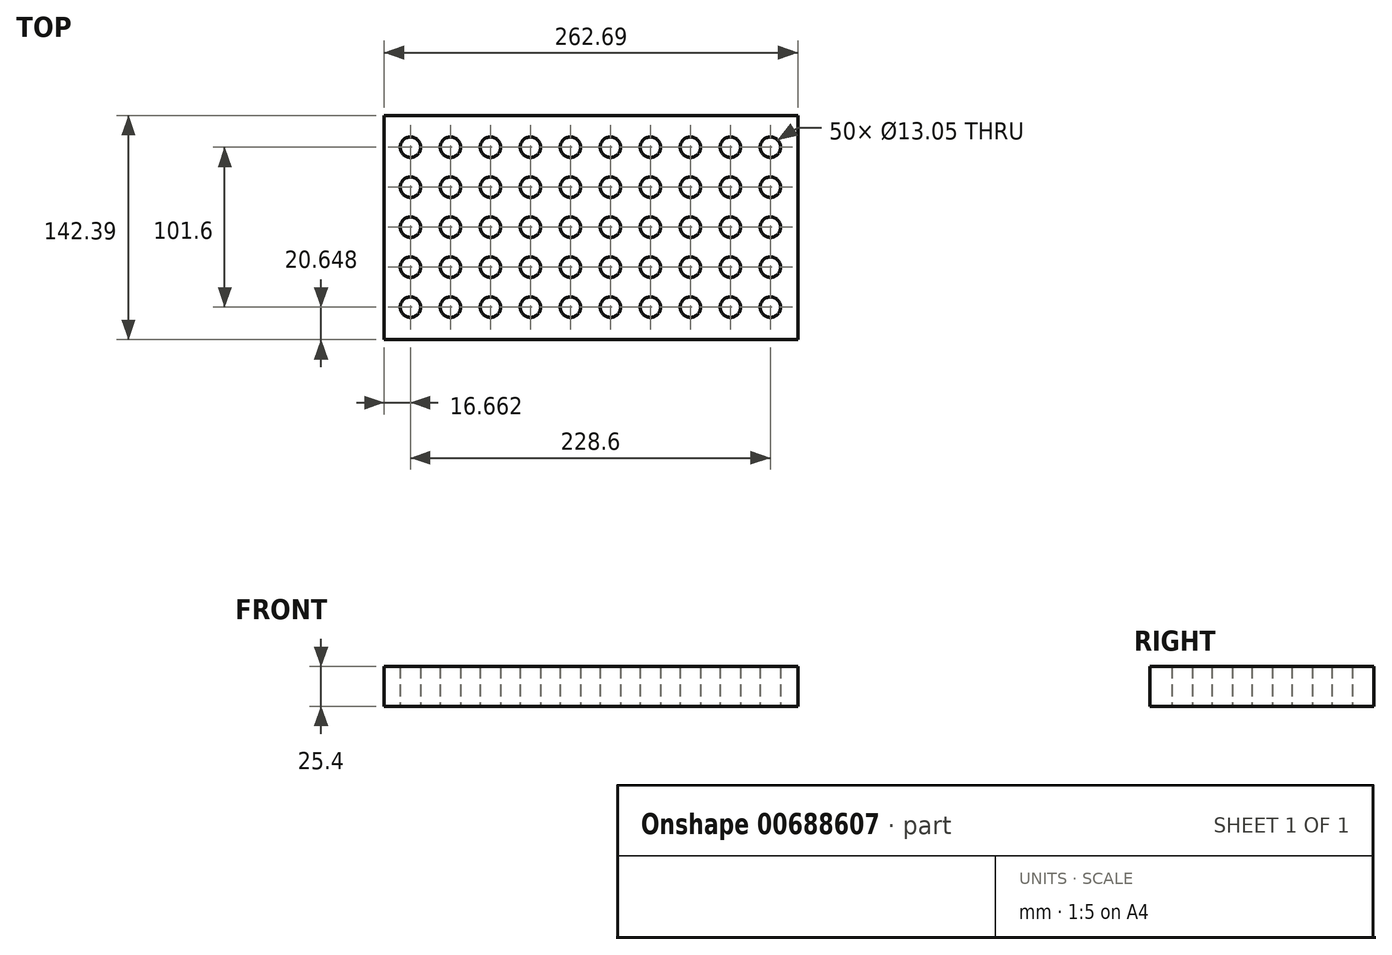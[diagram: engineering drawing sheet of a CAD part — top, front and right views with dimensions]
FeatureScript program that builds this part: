
annotation { "Feature Type Name" : "Feature", "Feature Type Description" : "" }
export const myFeature = defineFeature(function(context is Context, id is Id, definition is map)
    precondition{}
    {
        {
            var Q0;
            Q0=qCreatedBy(makeId("Top.planeOp"),FACE);
            var sketch = newSketch(context, id + "F0", { "sketchPlane" : qUnion([Q0])});
            skLineSegment(sketch, "E0.bottom", {"start": v(-134.73, 82.8) * mm, "end": v(127.96, 82.8) * mm});
            skLineSegment(sketch, "E0.top", {"start": v(-134.73, -59.6) * mm, "end": v(127.96, -59.6) * mm});
            skLineSegment(sketch, "E0.left", {"start": v(-134.73, 82.8) * mm, "end": v(-134.73, -59.6) * mm});
            skLineSegment(sketch, "E0.right", {"start": v(127.96, 82.8) * mm, "end": v(127.96, -59.6) * mm});
            skCircle(sketch, "E1", {"center": v(-118.07, -38.94) * mm, "radius": 6.52 * mm});
            skCircle(sketch, "E2.0.1.0", {"center": v(-118.07, -13.54) * mm, "radius": 6.52 * mm});
            skCircle(sketch, "E2.0.2.0", {"center": v(-118.07, 11.86) * mm, "radius": 6.52 * mm});
            skCircle(sketch, "E2.0.3.0", {"center": v(-118.07, 37.26) * mm, "radius": 6.52 * mm});
            skCircle(sketch, "E2.0.4.0", {"center": v(-118.07, 62.66) * mm, "radius": 6.52 * mm});
            skCircle(sketch, "E2.1.0.0", {"center": v(-92.67, -38.94) * mm, "radius": 6.52 * mm});
            skCircle(sketch, "E2.1.1.0", {"center": v(-92.67, -13.54) * mm, "radius": 6.52 * mm});
            skCircle(sketch, "E2.1.2.0", {"center": v(-92.67, 11.86) * mm, "radius": 6.52 * mm});
            skCircle(sketch, "E2.1.3.0", {"center": v(-92.67, 37.26) * mm, "radius": 6.52 * mm});
            skCircle(sketch, "E2.1.4.0", {"center": v(-92.67, 62.66) * mm, "radius": 6.52 * mm});
            skCircle(sketch, "E2.2.0.0", {"center": v(-67.27, -38.94) * mm, "radius": 6.52 * mm});
            skCircle(sketch, "E2.2.1.0", {"center": v(-67.27, -13.54) * mm, "radius": 6.52 * mm});
            skCircle(sketch, "E2.2.2.0", {"center": v(-67.27, 11.86) * mm, "radius": 6.52 * mm});
            skCircle(sketch, "E2.2.3.0", {"center": v(-67.27, 37.26) * mm, "radius": 6.52 * mm});
            skCircle(sketch, "E2.2.4.0", {"center": v(-67.27, 62.66) * mm, "radius": 6.52 * mm});
            skCircle(sketch, "E2.3.0.0", {"center": v(-41.87, -38.94) * mm, "radius": 6.52 * mm});
            skCircle(sketch, "E2.3.1.0", {"center": v(-41.87, -13.54) * mm, "radius": 6.52 * mm});
            skCircle(sketch, "E2.3.2.0", {"center": v(-41.87, 11.86) * mm, "radius": 6.52 * mm});
            skCircle(sketch, "E2.3.3.0", {"center": v(-41.87, 37.26) * mm, "radius": 6.52 * mm});
            skCircle(sketch, "E2.3.4.0", {"center": v(-41.87, 62.66) * mm, "radius": 6.52 * mm});
            skCircle(sketch, "E2.4.0.0", {"center": v(-16.47, -38.94) * mm, "radius": 6.52 * mm});
            skCircle(sketch, "E2.4.1.0", {"center": v(-16.47, -13.54) * mm, "radius": 6.52 * mm});
            skCircle(sketch, "E2.4.2.0", {"center": v(-16.47, 11.86) * mm, "radius": 6.52 * mm});
            skCircle(sketch, "E2.4.3.0", {"center": v(-16.47, 37.26) * mm, "radius": 6.52 * mm});
            skCircle(sketch, "E2.4.4.0", {"center": v(-16.47, 62.66) * mm, "radius": 6.52 * mm});
            skCircle(sketch, "E2.5.0.0", {"center": v(8.93, -38.94) * mm, "radius": 6.52 * mm});
            skCircle(sketch, "E2.5.1.0", {"center": v(8.93, -13.54) * mm, "radius": 6.52 * mm});
            skCircle(sketch, "E2.5.2.0", {"center": v(8.93, 11.86) * mm, "radius": 6.52 * mm});
            skCircle(sketch, "E2.5.3.0", {"center": v(8.93, 37.26) * mm, "radius": 6.52 * mm});
            skCircle(sketch, "E2.5.4.0", {"center": v(8.93, 62.66) * mm, "radius": 6.52 * mm});
            skCircle(sketch, "E2.6.0.0", {"center": v(34.33, -38.94) * mm, "radius": 6.52 * mm});
            skCircle(sketch, "E2.6.1.0", {"center": v(34.33, -13.54) * mm, "radius": 6.52 * mm});
            skCircle(sketch, "E2.6.2.0", {"center": v(34.33, 11.86) * mm, "radius": 6.52 * mm});
            skCircle(sketch, "E2.6.3.0", {"center": v(34.33, 37.26) * mm, "radius": 6.52 * mm});
            skCircle(sketch, "E2.6.4.0", {"center": v(34.33, 62.66) * mm, "radius": 6.52 * mm});
            skCircle(sketch, "E2.7.0.0", {"center": v(59.73, -38.94) * mm, "radius": 6.52 * mm});
            skCircle(sketch, "E2.7.1.0", {"center": v(59.73, -13.54) * mm, "radius": 6.52 * mm});
            skCircle(sketch, "E2.7.2.0", {"center": v(59.73, 11.86) * mm, "radius": 6.52 * mm});
            skCircle(sketch, "E2.7.3.0", {"center": v(59.73, 37.26) * mm, "radius": 6.52 * mm});
            skCircle(sketch, "E2.7.4.0", {"center": v(59.73, 62.66) * mm, "radius": 6.52 * mm});
            skCircle(sketch, "E2.8.0.0", {"center": v(85.13, -38.94) * mm, "radius": 6.52 * mm});
            skCircle(sketch, "E2.8.1.0", {"center": v(85.13, -13.54) * mm, "radius": 6.52 * mm});
            skCircle(sketch, "E2.8.2.0", {"center": v(85.13, 11.86) * mm, "radius": 6.52 * mm});
            skCircle(sketch, "E2.8.3.0", {"center": v(85.13, 37.26) * mm, "radius": 6.52 * mm});
            skCircle(sketch, "E2.8.4.0", {"center": v(85.13, 62.66) * mm, "radius": 6.52 * mm});
            skCircle(sketch, "E2.9.0.0", {"center": v(110.53, -38.94) * mm, "radius": 6.52 * mm});
            skCircle(sketch, "E2.9.1.0", {"center": v(110.53, -13.54) * mm, "radius": 6.52 * mm});
            skCircle(sketch, "E2.9.2.0", {"center": v(110.53, 11.86) * mm, "radius": 6.52 * mm});
            skCircle(sketch, "E2.9.3.0", {"center": v(110.53, 37.26) * mm, "radius": 6.52 * mm});
            skCircle(sketch, "E2.9.4.0", {"center": v(110.53, 62.66) * mm, "radius": 6.52 * mm});
            skLineSegment(sketch, "E2.direction1", {"start": v(-118.07, -38.94) * mm, "end": v(-92.67, -38.94) * mm, "construction": true});
            skLineSegment(sketch, "E2.direction2", {"start": v(-118.07, -38.94) * mm, "end": v(-118.07, -13.54) * mm, "construction": true});
            skSolve(sketch);
        }
        {
            var Q0;
            Q0=makeQuery(id+"F0.imprint","IMPRINT",FACE,{"disambiguationData":[TD([[makeQuery(id+"F0.imprint","IMPRINT",EDGE,{"derivedFrom":sQuery(id+"F0.wireOp",EDGE,"E0.bottom")}),-1.0]])]});
            extrude(context, id + "F1", {"entities" : qUnion([Q0]), "depth" : 25.4 * mm, "offsetDistance" : 25.4 * mm});
        }
    });
